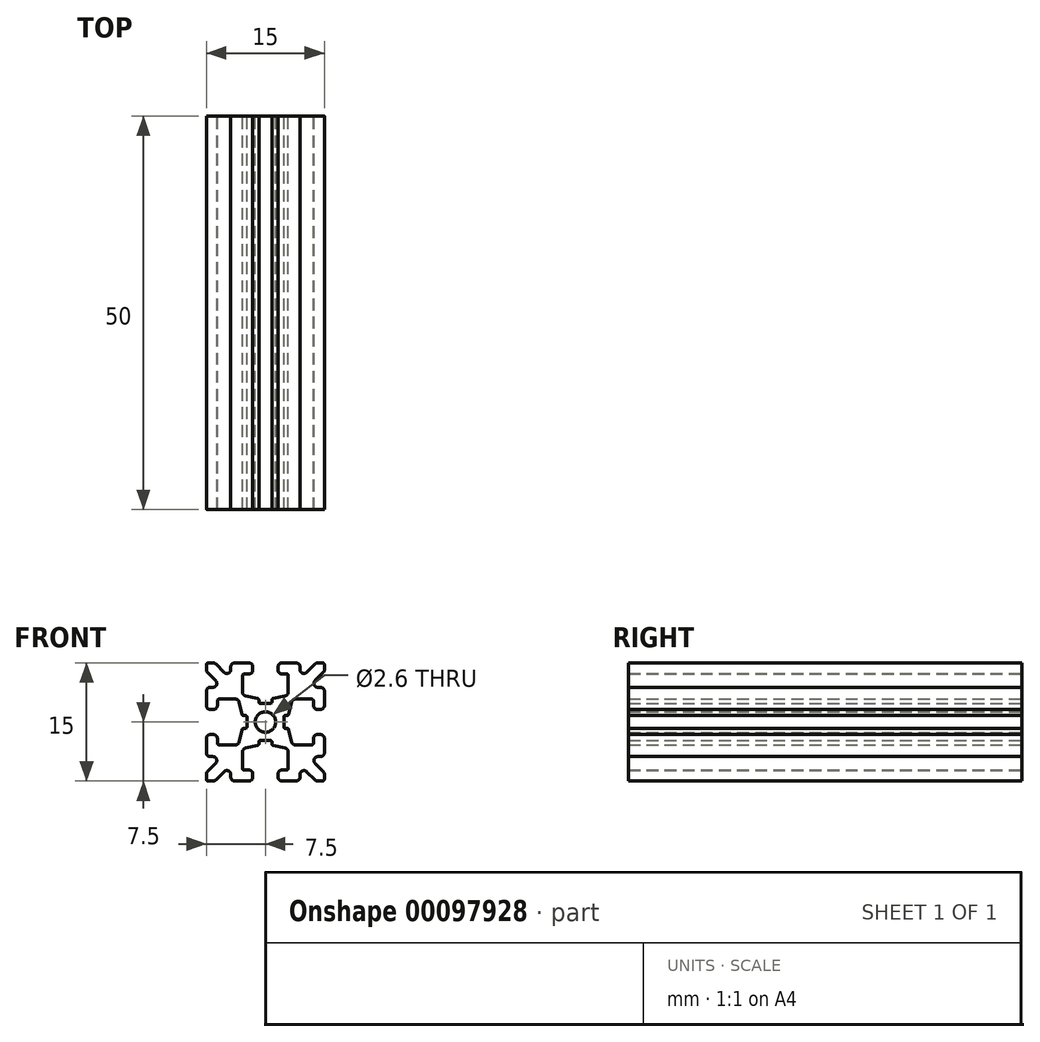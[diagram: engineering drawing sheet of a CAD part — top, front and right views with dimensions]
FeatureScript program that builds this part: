
annotation { "Feature Type Name" : "Feature", "Feature Type Description" : "" }
export const myFeature = defineFeature(function(context is Context, id is Id, definition is map)
    precondition{}
    {
        {
            var Q0;
            Q0=qCreatedBy(makeId("Front.planeOp"),FACE);
            var sketch = newSketch(context, id + "F0", { "sketchPlane" : qUnion([Q0])});
            skLineSegment(sketch, "E0.0.0", {"start": v(0.83, -2.55) * mm, "end": v(0.83, -2.77) * mm});
            skArc(sketch, "E0.0.1", {"start": v(0.83, -2.77) * mm, "mid": v(0.87, -2.9) * mm, "end": v(0.98, -2.97) * mm});
            skLineSegment(sketch, "E0.0.2", {"start": v(0.98, -2.97) * mm, "end": v(2.5, -3.31) * mm});
            skArc(sketch, "E0.0.3", {"start": v(2.5, -3.31) * mm, "mid": v(2.8, -3.49) * mm, "end": v(2.9, -3.8) * mm});
            skLineSegment(sketch, "E0.0.4", {"start": v(2.9, -3.8) * mm, "end": v(2.9, -5.9) * mm});
            skArc(sketch, "E0.0.5", {"start": v(2.9, -5.9) * mm, "mid": v(2.84, -6.04) * mm, "end": v(2.7, -6.1) * mm});
            skLineSegment(sketch, "E0.0.6", {"start": v(2.7, -6.1) * mm, "end": v(2.1, -6.1) * mm});
            skArc(sketch, "E0.0.7", {"start": v(2.1, -6.1) * mm, "mid": v(1.75, -6.25) * mm, "end": v(1.6, -6.6) * mm});
            skLineSegment(sketch, "E0.0.8", {"start": v(1.6, -6.6) * mm, "end": v(1.6, -7) * mm});
            skArc(sketch, "E0.0.9", {"start": v(1.6, -7) * mm, "mid": v(1.75, -7.35) * mm, "end": v(2.1, -7.5) * mm});
            skLineSegment(sketch, "E0.0.10", {"start": v(2.1, -7.5) * mm, "end": v(3.9, -7.5) * mm});
            skArc(sketch, "E0.0.11", {"start": v(3.9, -7.5) * mm, "mid": v(4.25, -7.35) * mm, "end": v(4.4, -7) * mm});
            skLineSegment(sketch, "E0.0.12", {"start": v(4.4, -7) * mm, "end": v(4.4, -6.67) * mm});
            skArc(sketch, "E0.0.13", {"start": v(4.4, -6.67) * mm, "mid": v(4.7, -6.2) * mm, "end": v(5.25, -6.31) * mm});
            skLineSegment(sketch, "E0.0.14", {"start": v(5.25, -6.31) * mm, "end": v(6.3, -7.35) * mm});
            skArc(sketch, "E0.0.15", {"start": v(6.3, -7.35) * mm, "mid": v(6.46, -7.46) * mm, "end": v(6.65, -7.5) * mm});
            skLineSegment(sketch, "E0.0.16", {"start": v(6.65, -7.5) * mm, "end": v(7.25, -7.5) * mm});
            skArc(sketch, "E0.0.17", {"start": v(7.25, -7.5) * mm, "mid": v(7.43, -7.43) * mm, "end": v(7.5, -7.25) * mm});
            skLineSegment(sketch, "E0.0.18", {"start": v(7.5, -7.25) * mm, "end": v(7.5, -6.65) * mm});
            skArc(sketch, "E0.0.19", {"start": v(7.5, -6.65) * mm, "mid": v(7.46, -6.46) * mm, "end": v(7.35, -6.3) * mm});
            skLineSegment(sketch, "E0.0.20", {"start": v(7.35, -6.3) * mm, "end": v(6.31, -5.25) * mm});
            skArc(sketch, "E0.0.21", {"start": v(6.31, -5.25) * mm, "mid": v(6.2, -4.7) * mm, "end": v(6.67, -4.4) * mm});
            skLineSegment(sketch, "E0.0.22", {"start": v(6.67, -4.4) * mm, "end": v(7, -4.4) * mm});
            skArc(sketch, "E0.0.23", {"start": v(7, -4.4) * mm, "mid": v(7.35, -4.25) * mm, "end": v(7.5, -3.9) * mm});
            skLineSegment(sketch, "E0.0.24", {"start": v(7.5, -3.9) * mm, "end": v(7.5, -2.1) * mm});
            skArc(sketch, "E0.0.25", {"start": v(7.5, -2.1) * mm, "mid": v(7.35, -1.75) * mm, "end": v(7, -1.6) * mm});
            skLineSegment(sketch, "E0.0.26", {"start": v(7, -1.6) * mm, "end": v(6.6, -1.6) * mm});
            skArc(sketch, "E0.0.27", {"start": v(6.6, -1.6) * mm, "mid": v(6.25, -1.75) * mm, "end": v(6.1, -2.1) * mm});
            skLineSegment(sketch, "E0.0.28", {"start": v(6.1, -2.1) * mm, "end": v(6.1, -2.7) * mm});
            skArc(sketch, "E0.0.29", {"start": v(6.1, -2.7) * mm, "mid": v(6.04, -2.84) * mm, "end": v(5.9, -2.9) * mm});
            skLineSegment(sketch, "E0.0.30", {"start": v(5.9, -2.9) * mm, "end": v(3.8, -2.9) * mm});
            skArc(sketch, "E0.0.31", {"start": v(3.8, -2.9) * mm, "mid": v(3.49, -2.8) * mm, "end": v(3.31, -2.5) * mm});
            skLineSegment(sketch, "E0.0.32", {"start": v(3.31, -2.5) * mm, "end": v(2.97, -0.98) * mm});
            skArc(sketch, "E0.0.33", {"start": v(2.97, -0.98) * mm, "mid": v(2.9, -0.87) * mm, "end": v(2.77, -0.83) * mm});
            skLineSegment(sketch, "E0.0.34", {"start": v(2.77, -0.83) * mm, "end": v(2.55, -0.83) * mm});
            skArc(sketch, "E0.0.35", {"start": v(2.55, -0.83) * mm, "mid": v(2.4, -0.77) * mm, "end": v(2.35, -0.63) * mm});
            skLineSegment(sketch, "E0.0.36", {"start": v(2.35, -0.63) * mm, "end": v(2.35, 0.63) * mm});
            skArc(sketch, "E0.0.37", {"start": v(2.35, 0.63) * mm, "mid": v(2.4, 0.77) * mm, "end": v(2.55, 0.83) * mm});
            skLineSegment(sketch, "E0.0.38", {"start": v(2.55, 0.83) * mm, "end": v(2.77, 0.83) * mm});
            skArc(sketch, "E0.0.39", {"start": v(2.77, 0.83) * mm, "mid": v(2.9, 0.87) * mm, "end": v(2.97, 0.98) * mm});
            skLineSegment(sketch, "E0.0.40", {"start": v(2.97, 0.98) * mm, "end": v(3.31, 2.5) * mm});
            skArc(sketch, "E0.0.41", {"start": v(3.31, 2.5) * mm, "mid": v(3.49, 2.8) * mm, "end": v(3.8, 2.9) * mm});
            skLineSegment(sketch, "E0.0.42", {"start": v(3.8, 2.9) * mm, "end": v(5.9, 2.9) * mm});
            skArc(sketch, "E0.0.43", {"start": v(5.9, 2.9) * mm, "mid": v(6.04, 2.84) * mm, "end": v(6.1, 2.7) * mm});
            skLineSegment(sketch, "E0.0.44", {"start": v(6.1, 2.7) * mm, "end": v(6.1, 2.1) * mm});
            skArc(sketch, "E0.0.45", {"start": v(6.1, 2.1) * mm, "mid": v(6.25, 1.75) * mm, "end": v(6.6, 1.6) * mm});
            skLineSegment(sketch, "E0.0.46", {"start": v(6.6, 1.6) * mm, "end": v(7, 1.6) * mm});
            skArc(sketch, "E0.0.47", {"start": v(7, 1.6) * mm, "mid": v(7.35, 1.75) * mm, "end": v(7.5, 2.1) * mm});
            skLineSegment(sketch, "E0.0.48", {"start": v(7.5, 2.1) * mm, "end": v(7.5, 3.9) * mm});
            skArc(sketch, "E0.0.49", {"start": v(7.5, 3.9) * mm, "mid": v(7.35, 4.25) * mm, "end": v(7, 4.4) * mm});
            skLineSegment(sketch, "E0.0.50", {"start": v(7, 4.4) * mm, "end": v(6.67, 4.4) * mm});
            skArc(sketch, "E0.0.51", {"start": v(6.67, 4.4) * mm, "mid": v(6.2, 4.7) * mm, "end": v(6.31, 5.25) * mm});
            skLineSegment(sketch, "E0.0.52", {"start": v(6.31, 5.25) * mm, "end": v(7.35, 6.3) * mm});
            skArc(sketch, "E0.0.53", {"start": v(7.35, 6.3) * mm, "mid": v(7.46, 6.46) * mm, "end": v(7.5, 6.65) * mm});
            skLineSegment(sketch, "E0.0.54", {"start": v(7.5, 6.65) * mm, "end": v(7.5, 7.25) * mm});
            skArc(sketch, "E0.0.55", {"start": v(7.5, 7.25) * mm, "mid": v(7.43, 7.43) * mm, "end": v(7.25, 7.5) * mm});
            skLineSegment(sketch, "E0.0.56", {"start": v(7.25, 7.5) * mm, "end": v(6.65, 7.5) * mm});
            skArc(sketch, "E0.0.57", {"start": v(6.65, 7.5) * mm, "mid": v(6.46, 7.46) * mm, "end": v(6.3, 7.35) * mm});
            skLineSegment(sketch, "E0.0.58", {"start": v(6.3, 7.35) * mm, "end": v(5.25, 6.31) * mm});
            skArc(sketch, "E0.0.59", {"start": v(5.25, 6.31) * mm, "mid": v(4.7, 6.2) * mm, "end": v(4.4, 6.67) * mm});
            skLineSegment(sketch, "E0.0.60", {"start": v(4.4, 6.67) * mm, "end": v(4.4, 7) * mm});
            skArc(sketch, "E0.0.61", {"start": v(4.4, 7) * mm, "mid": v(4.25, 7.35) * mm, "end": v(3.9, 7.5) * mm});
            skLineSegment(sketch, "E0.0.62", {"start": v(3.9, 7.5) * mm, "end": v(2.1, 7.5) * mm});
            skArc(sketch, "E0.0.63", {"start": v(2.1, 7.5) * mm, "mid": v(1.75, 7.35) * mm, "end": v(1.6, 7) * mm});
            skLineSegment(sketch, "E0.0.64", {"start": v(1.6, 7) * mm, "end": v(1.6, 6.6) * mm});
            skArc(sketch, "E0.0.65", {"start": v(1.6, 6.6) * mm, "mid": v(1.75, 6.25) * mm, "end": v(2.1, 6.1) * mm});
            skLineSegment(sketch, "E0.0.66", {"start": v(2.1, 6.1) * mm, "end": v(2.7, 6.1) * mm});
            skArc(sketch, "E0.0.67", {"start": v(2.7, 6.1) * mm, "mid": v(2.84, 6.04) * mm, "end": v(2.9, 5.9) * mm});
            skLineSegment(sketch, "E0.0.68", {"start": v(2.9, 5.9) * mm, "end": v(2.9, 3.8) * mm});
            skArc(sketch, "E0.0.69", {"start": v(2.9, 3.8) * mm, "mid": v(2.8, 3.49) * mm, "end": v(2.5, 3.31) * mm});
            skLineSegment(sketch, "E0.0.70", {"start": v(2.5, 3.31) * mm, "end": v(0.98, 2.97) * mm});
            skArc(sketch, "E0.0.71", {"start": v(0.98, 2.97) * mm, "mid": v(0.87, 2.9) * mm, "end": v(0.83, 2.77) * mm});
            skLineSegment(sketch, "E0.0.72", {"start": v(0.83, 2.77) * mm, "end": v(0.83, 2.55) * mm});
            skArc(sketch, "E0.0.73", {"start": v(0.83, 2.55) * mm, "mid": v(0.77, 2.4) * mm, "end": v(0.63, 2.35) * mm});
            skLineSegment(sketch, "E0.0.74", {"start": v(0.63, 2.35) * mm, "end": v(-0.63, 2.35) * mm});
            skArc(sketch, "E0.0.75", {"start": v(-0.63, 2.35) * mm, "mid": v(-0.77, 2.4) * mm, "end": v(-0.83, 2.55) * mm});
            skLineSegment(sketch, "E0.0.76", {"start": v(-0.83, 2.55) * mm, "end": v(-0.83, 2.77) * mm});
            skArc(sketch, "E0.0.77", {"start": v(-0.83, 2.77) * mm, "mid": v(-0.87, 2.9) * mm, "end": v(-0.98, 2.97) * mm});
            skLineSegment(sketch, "E0.0.78", {"start": v(-0.98, 2.97) * mm, "end": v(-2.5, 3.31) * mm});
            skArc(sketch, "E0.0.79", {"start": v(-2.5, 3.31) * mm, "mid": v(-2.8, 3.49) * mm, "end": v(-2.9, 3.8) * mm});
            skLineSegment(sketch, "E0.0.80", {"start": v(-2.9, 3.8) * mm, "end": v(-2.9, 5.9) * mm});
            skArc(sketch, "E0.0.81", {"start": v(-2.9, 5.9) * mm, "mid": v(-2.84, 6.04) * mm, "end": v(-2.7, 6.1) * mm});
            skLineSegment(sketch, "E0.0.82", {"start": v(-2.7, 6.1) * mm, "end": v(-2.1, 6.1) * mm});
            skArc(sketch, "E0.0.83", {"start": v(-2.1, 6.1) * mm, "mid": v(-1.75, 6.25) * mm, "end": v(-1.6, 6.6) * mm});
            skLineSegment(sketch, "E0.0.84", {"start": v(-1.6, 6.6) * mm, "end": v(-1.6, 7) * mm});
            skArc(sketch, "E0.0.85", {"start": v(-1.6, 7) * mm, "mid": v(-1.75, 7.35) * mm, "end": v(-2.1, 7.5) * mm});
            skLineSegment(sketch, "E0.0.86", {"start": v(-2.1, 7.5) * mm, "end": v(-3.9, 7.5) * mm});
            skArc(sketch, "E0.0.87", {"start": v(-3.9, 7.5) * mm, "mid": v(-4.25, 7.35) * mm, "end": v(-4.4, 7) * mm});
            skLineSegment(sketch, "E0.0.88", {"start": v(-4.4, 7) * mm, "end": v(-4.4, 6.67) * mm});
            skArc(sketch, "E0.0.89", {"start": v(-4.4, 6.67) * mm, "mid": v(-4.7, 6.2) * mm, "end": v(-5.25, 6.31) * mm});
            skLineSegment(sketch, "E0.0.90", {"start": v(-5.25, 6.31) * mm, "end": v(-6.3, 7.35) * mm});
            skArc(sketch, "E0.0.91", {"start": v(-6.3, 7.35) * mm, "mid": v(-6.46, 7.46) * mm, "end": v(-6.65, 7.5) * mm});
            skLineSegment(sketch, "E0.0.92", {"start": v(-6.65, 7.5) * mm, "end": v(-7.25, 7.5) * mm});
            skArc(sketch, "E0.0.93", {"start": v(-7.25, 7.5) * mm, "mid": v(-7.43, 7.43) * mm, "end": v(-7.5, 7.25) * mm});
            skLineSegment(sketch, "E0.0.94", {"start": v(-7.5, 7.25) * mm, "end": v(-7.5, 6.65) * mm});
            skArc(sketch, "E0.0.95", {"start": v(-7.5, 6.65) * mm, "mid": v(-7.46, 6.46) * mm, "end": v(-7.35, 6.3) * mm});
            skLineSegment(sketch, "E0.0.96", {"start": v(-7.35, 6.3) * mm, "end": v(-6.31, 5.25) * mm});
            skArc(sketch, "E0.0.97", {"start": v(-6.31, 5.25) * mm, "mid": v(-6.2, 4.7) * mm, "end": v(-6.67, 4.4) * mm});
            skLineSegment(sketch, "E0.0.98", {"start": v(-6.67, 4.4) * mm, "end": v(-7, 4.4) * mm});
            skArc(sketch, "E0.0.99", {"start": v(-7, 4.4) * mm, "mid": v(-7.35, 4.25) * mm, "end": v(-7.5, 3.9) * mm});
            skLineSegment(sketch, "E0.0.100", {"start": v(-7.5, 3.9) * mm, "end": v(-7.5, 2.1) * mm});
            skArc(sketch, "E0.0.101", {"start": v(-7.5, 2.1) * mm, "mid": v(-7.35, 1.75) * mm, "end": v(-7, 1.6) * mm});
            skLineSegment(sketch, "E0.0.102", {"start": v(-7, 1.6) * mm, "end": v(-6.6, 1.6) * mm});
            skArc(sketch, "E0.0.103", {"start": v(-6.6, 1.6) * mm, "mid": v(-6.25, 1.75) * mm, "end": v(-6.1, 2.1) * mm});
            skLineSegment(sketch, "E0.0.104", {"start": v(-6.1, 2.1) * mm, "end": v(-6.1, 2.7) * mm});
            skArc(sketch, "E0.0.105", {"start": v(-6.1, 2.7) * mm, "mid": v(-6.04, 2.84) * mm, "end": v(-5.9, 2.9) * mm});
            skLineSegment(sketch, "E0.0.106", {"start": v(-5.9, 2.9) * mm, "end": v(-3.8, 2.9) * mm});
            skArc(sketch, "E0.0.107", {"start": v(-3.8, 2.9) * mm, "mid": v(-3.49, 2.8) * mm, "end": v(-3.31, 2.5) * mm});
            skLineSegment(sketch, "E0.0.108", {"start": v(-3.31, 2.5) * mm, "end": v(-2.97, 0.98) * mm});
            skArc(sketch, "E0.0.109", {"start": v(-2.97, 0.98) * mm, "mid": v(-2.9, 0.87) * mm, "end": v(-2.77, 0.83) * mm});
            skLineSegment(sketch, "E0.0.110", {"start": v(-2.77, 0.83) * mm, "end": v(-2.55, 0.83) * mm});
            skArc(sketch, "E0.0.111", {"start": v(-2.55, 0.83) * mm, "mid": v(-2.4, 0.77) * mm, "end": v(-2.35, 0.63) * mm});
            skLineSegment(sketch, "E0.0.112", {"start": v(-2.35, 0.63) * mm, "end": v(-2.35, -0.63) * mm});
            skArc(sketch, "E0.0.113", {"start": v(-2.35, -0.63) * mm, "mid": v(-2.4, -0.77) * mm, "end": v(-2.55, -0.83) * mm});
            skLineSegment(sketch, "E0.0.114", {"start": v(-2.55, -0.83) * mm, "end": v(-2.77, -0.83) * mm});
            skArc(sketch, "E0.0.115", {"start": v(-2.77, -0.83) * mm, "mid": v(-2.9, -0.87) * mm, "end": v(-2.97, -0.98) * mm});
            skLineSegment(sketch, "E0.0.116", {"start": v(-2.97, -0.98) * mm, "end": v(-3.31, -2.5) * mm});
            skArc(sketch, "E0.0.117", {"start": v(-3.31, -2.5) * mm, "mid": v(-3.49, -2.8) * mm, "end": v(-3.8, -2.9) * mm});
            skLineSegment(sketch, "E0.0.118", {"start": v(-3.8, -2.9) * mm, "end": v(-5.9, -2.9) * mm});
            skArc(sketch, "E0.0.119", {"start": v(-5.9, -2.9) * mm, "mid": v(-6.04, -2.84) * mm, "end": v(-6.1, -2.7) * mm});
            skLineSegment(sketch, "E0.0.120", {"start": v(-6.1, -2.7) * mm, "end": v(-6.1, -2.1) * mm});
            skArc(sketch, "E0.0.121", {"start": v(-6.1, -2.1) * mm, "mid": v(-6.25, -1.75) * mm, "end": v(-6.6, -1.6) * mm});
            skLineSegment(sketch, "E0.0.122", {"start": v(-6.6, -1.6) * mm, "end": v(-7, -1.6) * mm});
            skArc(sketch, "E0.0.123", {"start": v(-7, -1.6) * mm, "mid": v(-7.35, -1.75) * mm, "end": v(-7.5, -2.1) * mm});
            skLineSegment(sketch, "E0.0.124", {"start": v(-7.5, -2.1) * mm, "end": v(-7.5, -3.9) * mm});
            skArc(sketch, "E0.0.125", {"start": v(-7.5, -3.9) * mm, "mid": v(-7.35, -4.25) * mm, "end": v(-7, -4.4) * mm});
            skLineSegment(sketch, "E0.0.126", {"start": v(-7, -4.4) * mm, "end": v(-6.67, -4.4) * mm});
            skArc(sketch, "E0.0.127", {"start": v(-6.67, -4.4) * mm, "mid": v(-6.2, -4.7) * mm, "end": v(-6.31, -5.25) * mm});
            skLineSegment(sketch, "E0.0.128", {"start": v(-6.31, -5.25) * mm, "end": v(-7.35, -6.3) * mm});
            skArc(sketch, "E0.0.129", {"start": v(-7.35, -6.3) * mm, "mid": v(-7.46, -6.46) * mm, "end": v(-7.5, -6.65) * mm});
            skLineSegment(sketch, "E0.0.130", {"start": v(-7.5, -6.65) * mm, "end": v(-7.5, -7.25) * mm});
            skArc(sketch, "E0.0.131", {"start": v(-7.5, -7.25) * mm, "mid": v(-7.43, -7.43) * mm, "end": v(-7.25, -7.5) * mm});
            skLineSegment(sketch, "E0.0.132", {"start": v(-7.25, -7.5) * mm, "end": v(-6.65, -7.5) * mm});
            skArc(sketch, "E0.0.133", {"start": v(-6.65, -7.5) * mm, "mid": v(-6.46, -7.46) * mm, "end": v(-6.3, -7.35) * mm});
            skLineSegment(sketch, "E0.0.134", {"start": v(-6.3, -7.35) * mm, "end": v(-5.25, -6.31) * mm});
            skArc(sketch, "E0.0.135", {"start": v(-5.25, -6.31) * mm, "mid": v(-4.7, -6.2) * mm, "end": v(-4.4, -6.67) * mm});
            skLineSegment(sketch, "E0.0.136", {"start": v(-4.4, -6.67) * mm, "end": v(-4.4, -7) * mm});
            skArc(sketch, "E0.0.137", {"start": v(-4.4, -7) * mm, "mid": v(-4.25, -7.35) * mm, "end": v(-3.9, -7.5) * mm});
            skLineSegment(sketch, "E0.0.138", {"start": v(-3.9, -7.5) * mm, "end": v(-2.1, -7.5) * mm});
            skArc(sketch, "E0.0.139", {"start": v(-2.1, -7.5) * mm, "mid": v(-1.75, -7.35) * mm, "end": v(-1.6, -7) * mm});
            skLineSegment(sketch, "E0.0.140", {"start": v(-1.6, -7) * mm, "end": v(-1.6, -6.6) * mm});
            skArc(sketch, "E0.0.141", {"start": v(-1.6, -6.6) * mm, "mid": v(-1.75, -6.25) * mm, "end": v(-2.1, -6.1) * mm});
            skLineSegment(sketch, "E0.0.142", {"start": v(-2.1, -6.1) * mm, "end": v(-2.7, -6.1) * mm});
            skArc(sketch, "E0.0.143", {"start": v(-2.7, -6.1) * mm, "mid": v(-2.84, -6.04) * mm, "end": v(-2.9, -5.9) * mm});
            skLineSegment(sketch, "E0.0.144", {"start": v(-2.9, -5.9) * mm, "end": v(-2.9, -3.8) * mm});
            skArc(sketch, "E0.0.145", {"start": v(-2.9, -3.8) * mm, "mid": v(-2.8, -3.49) * mm, "end": v(-2.5, -3.31) * mm});
            skLineSegment(sketch, "E0.0.146", {"start": v(-2.5, -3.31) * mm, "end": v(-0.98, -2.97) * mm});
            skArc(sketch, "E0.0.147", {"start": v(-0.98, -2.97) * mm, "mid": v(-0.87, -2.9) * mm, "end": v(-0.83, -2.77) * mm});
            skLineSegment(sketch, "E0.0.148", {"start": v(-0.83, -2.77) * mm, "end": v(-0.83, -2.55) * mm});
            skArc(sketch, "E0.0.149", {"start": v(-0.83, -2.55) * mm, "mid": v(-0.77, -2.4) * mm, "end": v(-0.63, -2.35) * mm});
            skLineSegment(sketch, "E0.0.150", {"start": v(-0.63, -2.35) * mm, "end": v(0.63, -2.35) * mm});
            skArc(sketch, "E0.0.151", {"start": v(0.63, -2.35) * mm, "mid": v(0.77, -2.4) * mm, "end": v(0.83, -2.55) * mm});
            skPoint(sketch, "E1", {"position": v(0, 0) * mm});
            skPoint(sketch, "E1.positionSnap0", {"position": v(0, 2.35) * mm});
            skPoint(sketch, "E1.positionSnap1", {"position": v(2.35, 0) * mm});
            skCircle(sketch, "E2", {"center": v(0, 0) * mm, "radius": 1.3 * mm});
            skSolve(sketch);
        }
        {
            var Q0;
            Q0=makeQuery(id+"F0.imprint","IMPRINT",FACE,{"disambiguationData":[TD([[makeQuery(id+"F0.imprint","IMPRINT",EDGE,{"derivedFrom":sQuery(id+"F0.wireOp",EDGE,"E0.0.0")}),1.0]])]});
            extrude(context, id + "F1", {"entities" : qUnion([Q0]), "endBound" : BoundingType.SYMMETRIC, "depth" : 50 * mm});
        }
    });
